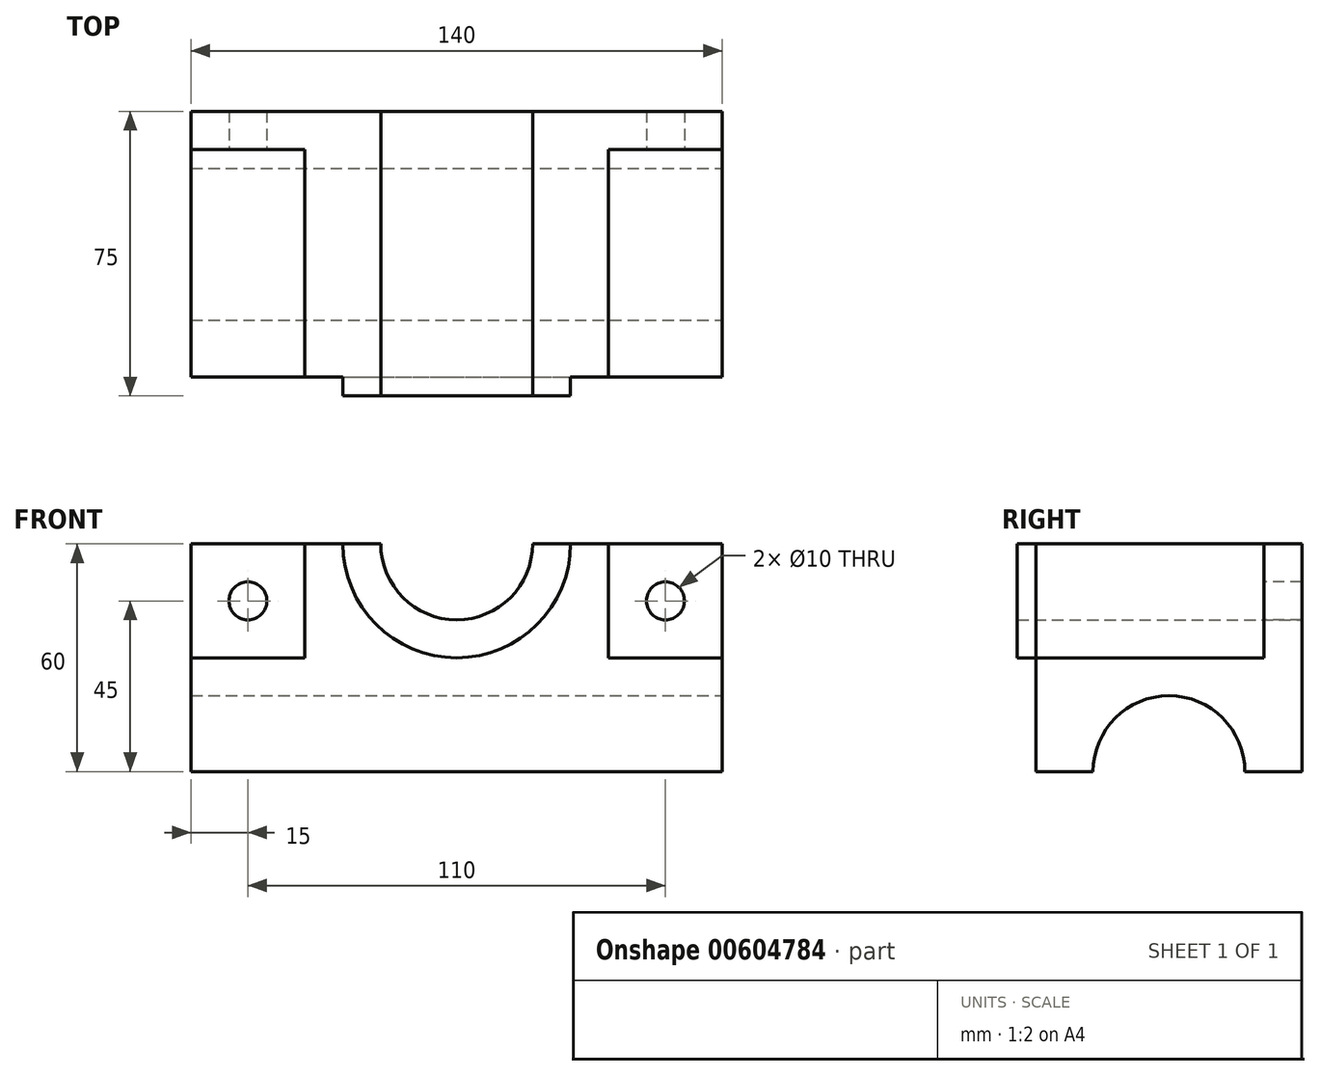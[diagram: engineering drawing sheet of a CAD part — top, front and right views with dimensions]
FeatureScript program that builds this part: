
annotation { "Feature Type Name" : "Feature", "Feature Type Description" : "" }
export const myFeature = defineFeature(function(context is Context, id is Id, definition is map)
    precondition{}
    {
        {
            var Q0;
            Q0=qCreatedBy(makeId("Front.planeOp"),FACE);
            var sketch = newSketch(context, id + "F0", { "sketchPlane" : qUnion([Q0])});
            skLineSegment(sketch, "E0.bottom", {"start": v(0, 0) * mm, "end": v(70, 0) * mm});
            skLineSegment(sketch, "E0.top", {"start": v(20, 60) * mm, "end": v(70, 60) * mm});
            skLineSegment(sketch, "E0.left", {"start": v(0, 0) * mm, "end": v(0, 40) * mm});
            skLineSegment(sketch, "E0.right", {"start": v(70, 0) * mm, "end": v(70, 60) * mm});
            skArc(sketch, "E1", {"start": v(0, 40) * mm, "mid": v(14.14, 45.86) * mm, "end": v(20, 60) * mm});
            skArc(sketch, "E2.0", {"start": v(0, 30) * mm, "mid": v(21.21, 38.79) * mm, "end": v(30, 60) * mm});
            skSolve(sketch);
        }
        {
            var Q0;
            Q0=makeQuery(id+"F0.imprint","IMPRINT",FACE,{"disambiguationData":[TD([[makeQuery(id+"F0.imprint","IMPRINT",EDGE,{"derivedFrom":sQuery(id+"F0.wireOp",EDGE,"E0.bottom")}),1.0]])]});
            var Q1;
            {var subQ0=sQuery(id+"F0.wireOp",EDGE,"E1");Q1=makeQuery(id+"F0.imprint","IMPRINT",FACE,{"disambiguationData":[TD([[makeQuery(id+"F0.imprint","IMPRINT",EDGE,{"derivedFrom":subQ0}),-1.0]])]});}
            extrude(context, id + "F1", {"entities" : qUnion([Q0, Q1]), "depth" : 70 * mm, "offsetDistance" : 25 * mm, "symmetric" : true});
        }
        {
            var Q0;
            Q0=makeQuery(id+"F1.opExtrude","CAP_FACE",FACE,{"disambiguationData":[OSD([sQuery(id+"F0.wireOp",EDGE,"E0.bottom"),sQuery(id+"F0.wireOp",EDGE,"E0.top"),sQuery(id+"F0.wireOp",EDGE,"E0.left"),sQuery(id+"F0.wireOp",EDGE,"E0.right"),sQuery(id+"F0.wireOp",EDGE,"E1")])],"isStart":false});
            var sketch = newSketch(context, id + "F2", { "sketchPlane" : qUnion([Q0])});
            skLineSegment(sketch, "E3.bottom", {"start": v(70, 60) * mm, "end": v(40, 60) * mm});
            skLineSegment(sketch, "E3.top", {"start": v(70, 30) * mm, "end": v(40, 30) * mm});
            skLineSegment(sketch, "E3.left", {"start": v(70, 60) * mm, "end": v(70, 30) * mm});
            skLineSegment(sketch, "E3.right", {"start": v(40, 60) * mm, "end": v(40, 30) * mm});
            skSolve(sketch);
        }
        {
            var Q0;
            Q0=makeQuery(id+"F2.imprint","IMPRINT",FACE,{"disambiguationData":[TD([[makeQuery(id+"F2.imprint","IMPRINT",EDGE,{"derivedFrom":sQuery(id+"F2.wireOp",EDGE,"E3.bottom")}),-1.0]])]});
            extrude(context, id + "F3", {"entities" : qUnion([Q0]), "operationType" : NewBodyOperationType.REMOVE, "oppositeDirection" : true, "depth" : 60 * mm, "offsetDistance" : 25 * mm});
        }
        {
            var Q0;
            Q0=makeQuery(id+"F3.boolean.opBoolean","COPY",FACE,{"derivedFrom":makeQuery(id+"F3.opExtrude","CAP_FACE",FACE,{"disambiguationData":[OSD([sQuery(id+"F2.wireOp",EDGE,"E3.bottom"),sQuery(id+"F2.wireOp",EDGE,"E3.top"),sQuery(id+"F2.wireOp",EDGE,"E3.left"),sQuery(id+"F2.wireOp",EDGE,"E3.right")])],"isStart":false})});
            var sketch = newSketch(context, id + "F4", { "sketchPlane" : qUnion([Q0])});
            skCircle(sketch, "E4", {"center": v(55, 45) * mm, "radius": 5 * mm});
            skPoint(sketch, "E4.centerSnap0", {"position": v(70, 45) * mm});
            skPoint(sketch, "E4.centerSnap1", {"position": v(55, 60) * mm});
            skSolve(sketch);
        }
        {
            var Q0;
            Q0=makeQuery(id+"F4.imprint","IMPRINT",FACE,{"disambiguationData":[TD([[makeQuery(id+"F4.imprint","IMPRINT",EDGE,{"derivedFrom":sQuery(id+"F4.wireOp",EDGE,"E4")}),1.0]])]});
            extrude(context, id + "F5", {"entities" : qUnion([Q0]), "operationType" : NewBodyOperationType.REMOVE, "endBound" : BoundingType.THROUGH_ALL, "oppositeDirection" : true, "depth" : 25 * mm, "offsetDistance" : 25 * mm});
        }
        {
            var Q0;
            Q0=makeQuery(id+"F1.opExtrude","SWEPT_FACE",FACE,{"disambiguationData":[OSD([sQuery(id+"F0.wireOp",EDGE,"E0.right")])]});
            var sketch = newSketch(context, id + "F6", { "sketchPlane" : qUnion([Q0])});
            skArc(sketch, "E5", {"start": v(20, 0) * mm, "mid": v(0, 20) * mm, "end": v(-20, 0) * mm});
            skPoint(sketch, "E6", {"position": v(-20, 0) * mm});
            skPoint(sketch, "E7", {"position": v(20, 0) * mm});
            skSolve(sketch);
        }
        {
            var Q0;
            {var subQ0=sQuery(id+"F6.wireOp",EDGE,"E5");Q0=makeQuery(id+"F6.imprint","IMPRINT",FACE,{"disambiguationData":[TD([[makeQuery(id+"F6.imprint","IMPRINT",EDGE,{"derivedFrom":subQ0}),1.0]])]});}
            extrude(context, id + "F7", {"entities" : qUnion([Q0]), "operationType" : NewBodyOperationType.REMOVE, "endBound" : BoundingType.THROUGH_ALL, "oppositeDirection" : true, "depth" : 25 * mm, "offsetDistance" : 25 * mm});
        }
        {
            var Q0;
            {var subQ0=sQuery(id+"F0.wireOp",EDGE,"E1");Q0=makeQuery(id+"F0.imprint","IMPRINT",FACE,{"disambiguationData":[TD([[makeQuery(id+"F0.imprint","IMPRINT",EDGE,{"derivedFrom":subQ0}),-1.0]])]});}
            extrude(context, id + "F8", {"entities" : qUnion([Q0]), "operationType" : NewBodyOperationType.ADD, "depth" : 40 * mm, "offsetDistance" : 25 * mm});
        }
        {
            var Q0;
            Q0=makeQuery(id+"F1.opExtrude","SWEPT_BODY",BODY,{"disambiguationData":[OSD([sQuery(id+"F0.wireOp",EDGE,"E0.bottom"),sQuery(id+"F0.wireOp",EDGE,"E0.top"),sQuery(id+"F0.wireOp",EDGE,"E0.left"),sQuery(id+"F0.wireOp",EDGE,"E0.right"),sQuery(id+"F0.wireOp",EDGE,"E1")])]});
            var Q1;
            Q1=qCreatedBy(makeId("Right.planeOp"),FACE);
            mirror(context, id + "F9", {"operationType" : NewBodyOperationType.ADD, "entities" : qUnion([Q0]), "mirrorPlane" : qUnion([Q1])});
        }
    });
